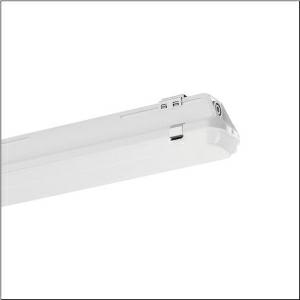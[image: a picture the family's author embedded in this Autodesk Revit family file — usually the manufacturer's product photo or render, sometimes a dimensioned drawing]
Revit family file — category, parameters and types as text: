
# Revit family: monsun_r__21_51fb10dp460c_27a0
name_source: partatom
category: Lighting Fixtures
units: mm (PartAtom-declared; Revit-internal decimal feet)

## family parameters
Cut with Voids When Loaded = No
Host = Face
Light Source = No
Part Type = Normal
Room Calculation Point = No
Round Connector Dimension = Use Diameter
Shared = No

## types (1)
- --- (1 x LED, 6060 lm, 32.7 W, 4000K)
    Apparent Load = 33 VA
    CIE Flux Codes = 47 77 93 94 100
    Color Rendering = 80
    Color Temperature = 4000K
    Default Elevation = 1800 mm
    Description = Monsun® 21, damp-proof luminaire, chain hanger, primary optical cover: enclosure, of PMMA, light emission: direct distribution, primary light characteristic: symmetric, installation type: suspended mounting, surface-mounted, horizontal mounting, vertical mounting, LED, rated luminous flux: 6.060lm, luminous efficacy: 185lm/W, light colour: 840, colour temperature: 4000K, control gear: DALI 2, with terminal, 5-pole, max. 2.5mm², mains connection: 220..240V, AC, 50/60Hz, rated input power: 33W, housing, of glass-fibre reinforced polyester, uncoated, bright grey, incl. chain hanger, length: 1.590mm, width: 90mm, height: 88mm, clip for enclosure, of stainless steel (V2A), ceiling mounting element, of stainless steel (V2A), chain hanger, of stainless steel (V2A), protection rating (complete): IP66, insulation class (complete): insulation class I (protective earthing), certification: CE, ENEC, VDE, UKCA, protection symbol: D, impact resistance: IK04, permissible operating ambient temperature: -25..+35°C, standard: EN 50419, EN 60598-2-1, corresponds to IFS (International Featured Standards) requirements for safety and quality in the food industry, for indoor or canopied outdoor use, no direct snow, no direct sun, no direct rain, LABS conformity tested according to VDMA 24364:2018-05, contact your sales advisor before using the luminaires in applications with unclear chemical exposure, large temperature fluctuations or condensation-forming humidity, packaging unit: 1 piece
    Height = 89 mm
    Lamp = 1 x LED
    Lamp Light Flux = 6060 lm
    Lamp Power = 32.7 W
    Lamp count = 1
    Length = 1590 mm
    Luminous efficacy = 185 lm/W
    Manufacturer = Siteco
    ModVariant = No
    Model = 51FB10DP460C
    Mounting Place = Ceiling
    Mounting Type = Surface mounted
    Number of Poles = 1
    OnlyDefault = Yes
    Power Factor = 1
    Product Name = Monsun® 21
    Product group = damp-proof luminaire
    ProductGroupID = 301
    Protection Class = Protection class I
    Protection Degree = IP 66
    RLX_Detail_Level = 1
    RLX_Emergency_Light_Flux = 0 lm
    RLX_Emergency_Type = 0
    RLX_Emergency_Type_DB = No
    RlxData = <blob elided: 92481 chars, md5=e536ad03>
    Socket = socket
    Standby Power = 0 W
    System Light Flux = 6060 lm
    System Power = 33 W
    Type Comments = factory setting: luminous flux: 100 % | dim-lin: 254 | 229 mA
    Type Image = l_1319656.jpg
    URL = http://relux.com
    VarID = @adj_051965
    Voltage = 0 V
    Weight = 0.00 kg
    Width = 90 mm

## geometry (parser evidence)
native form markers: Blend x4, Sweep x12
no freeform markers — native parametric forms only
